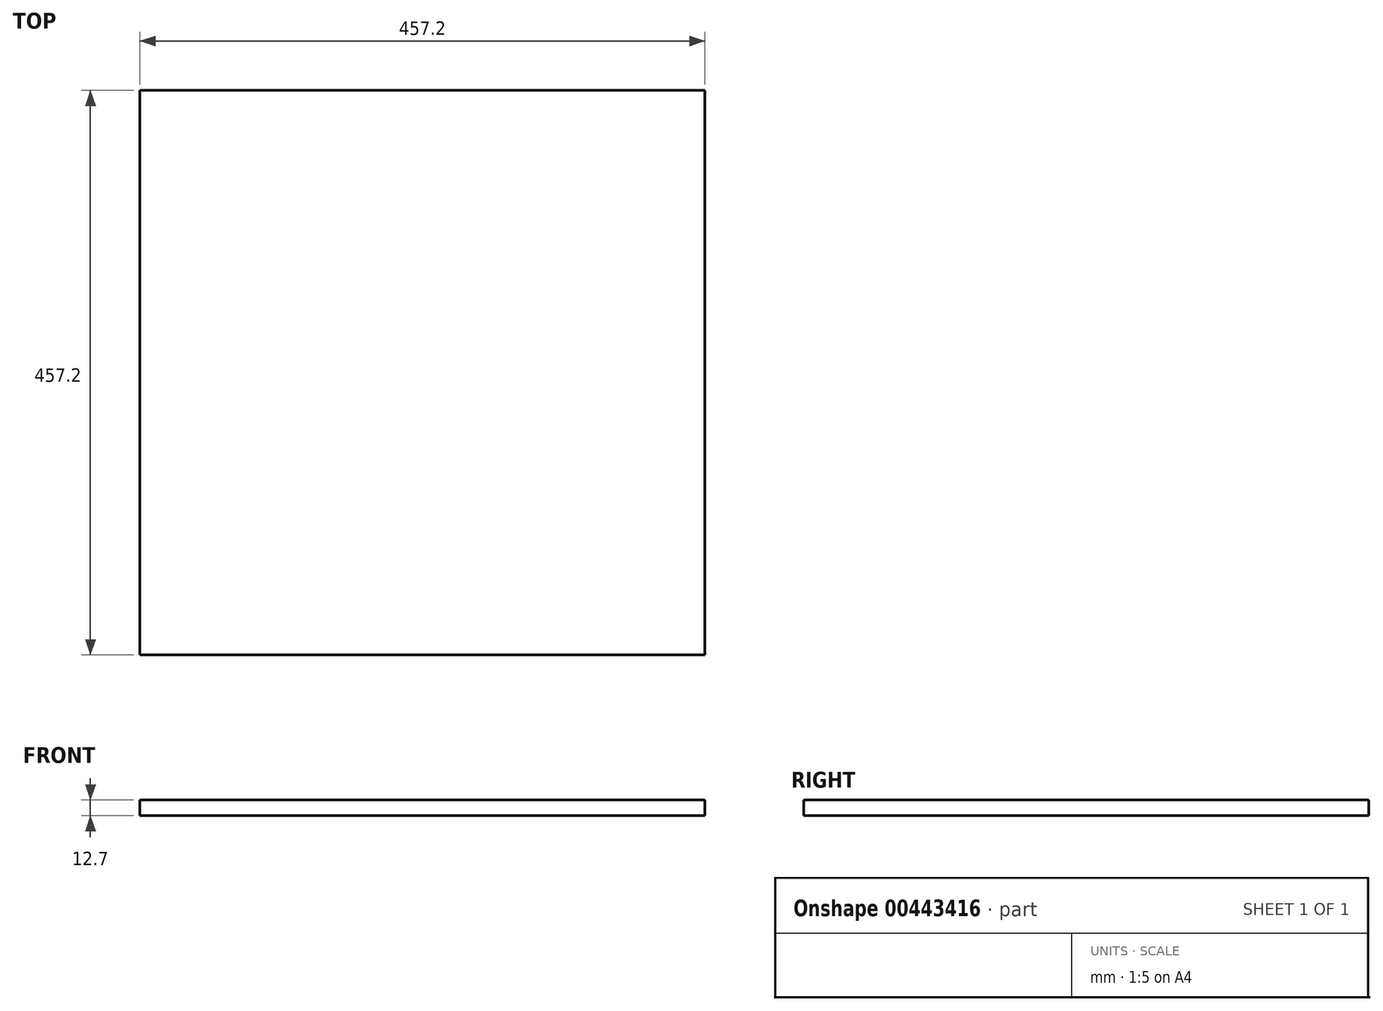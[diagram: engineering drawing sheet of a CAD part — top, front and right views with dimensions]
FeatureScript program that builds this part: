
annotation { "Feature Type Name" : "Feature", "Feature Type Description" : "" }
export const myFeature = defineFeature(function(context is Context, id is Id, definition is map)
    precondition{}
    {
        {
            var Q0;
            Q0=qCreatedBy(makeId("Top.planeOp"),FACE);
            var sketch = newSketch(context, id + "F0", { "sketchPlane" : qUnion([Q0])});
            skLineSegment(sketch, "E0.bottom", {"start": v(228.6, -228.6) * mm, "end": v(-228.6, -228.6) * mm});
            skLineSegment(sketch, "E0.top", {"start": v(228.6, 228.6) * mm, "end": v(-228.6, 228.6) * mm});
            skLineSegment(sketch, "E0.left", {"start": v(228.6, -228.6) * mm, "end": v(228.6, 228.6) * mm});
            skLineSegment(sketch, "E0.right", {"start": v(-228.6, -228.6) * mm, "end": v(-228.6, 228.6) * mm});
            skPoint(sketch, "E0.middle", {"position": v(0, 0) * mm});
            skSolve(sketch);
        }
        {
            var Q0;
            Q0 = qSketchRegion(id + "F0", true);
            extrude(context, id + "F1", {"entities" : qUnion([Q0]), "depth" : 12.7 * mm});
        }
    });
